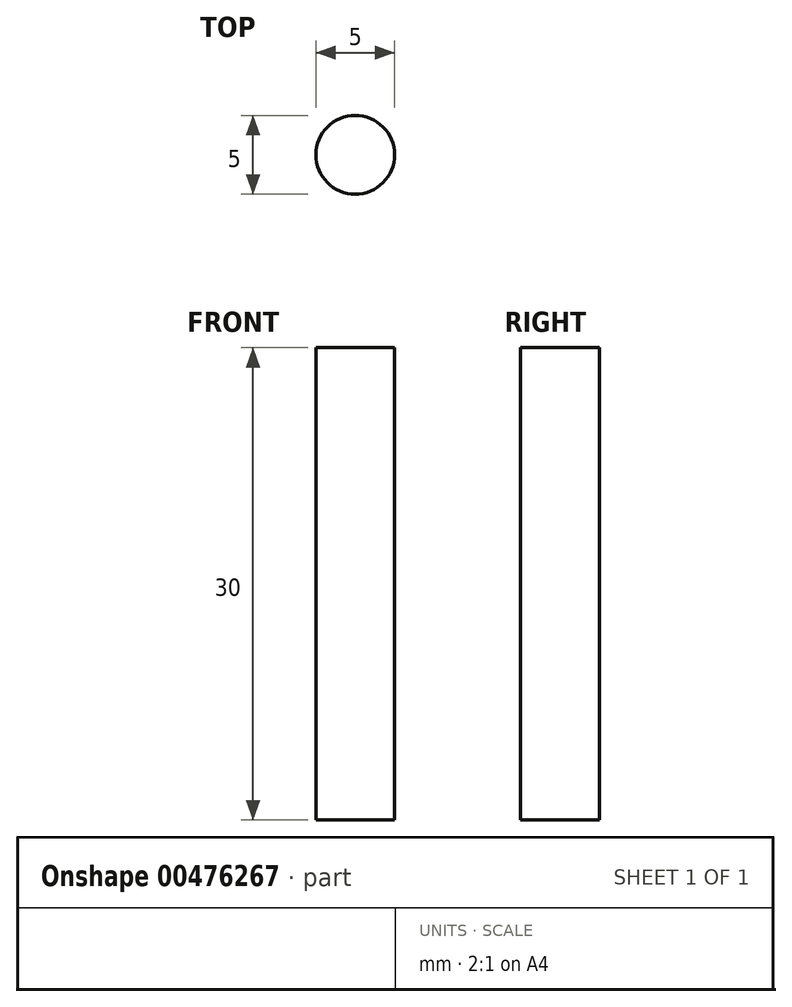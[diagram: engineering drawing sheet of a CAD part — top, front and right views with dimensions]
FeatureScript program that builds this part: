
annotation { "Feature Type Name" : "Feature", "Feature Type Description" : "" }
export const myFeature = defineFeature(function(context is Context, id is Id, definition is map)
    precondition{}
    {
        {
            var Q0;
            Q0=qCreatedBy(makeId("Top.planeOp"),FACE);
            var sketch = newSketch(context, id + "F0", { "sketchPlane" : qUnion([Q0])});
            skCircle(sketch, "E0", {"center": v(31.2, 30.7) * mm, "radius": 2.5 * mm});
            skSolve(sketch);
        }
        {
            var Q0;
            Q0=makeQuery(id+"F0.imprint","IMPRINT",FACE,{"disambiguationData":[TD([[makeQuery(id+"F0.imprint","IMPRINT",EDGE,{"derivedFrom":sQuery(id+"F0.wireOp",EDGE,"E0")}),1.0]])]});
            extrude(context, id + "F1", {"entities" : qUnion([Q0]), "depth" : 30 * mm, "offsetDistance" : 25 * mm});
        }
    });
